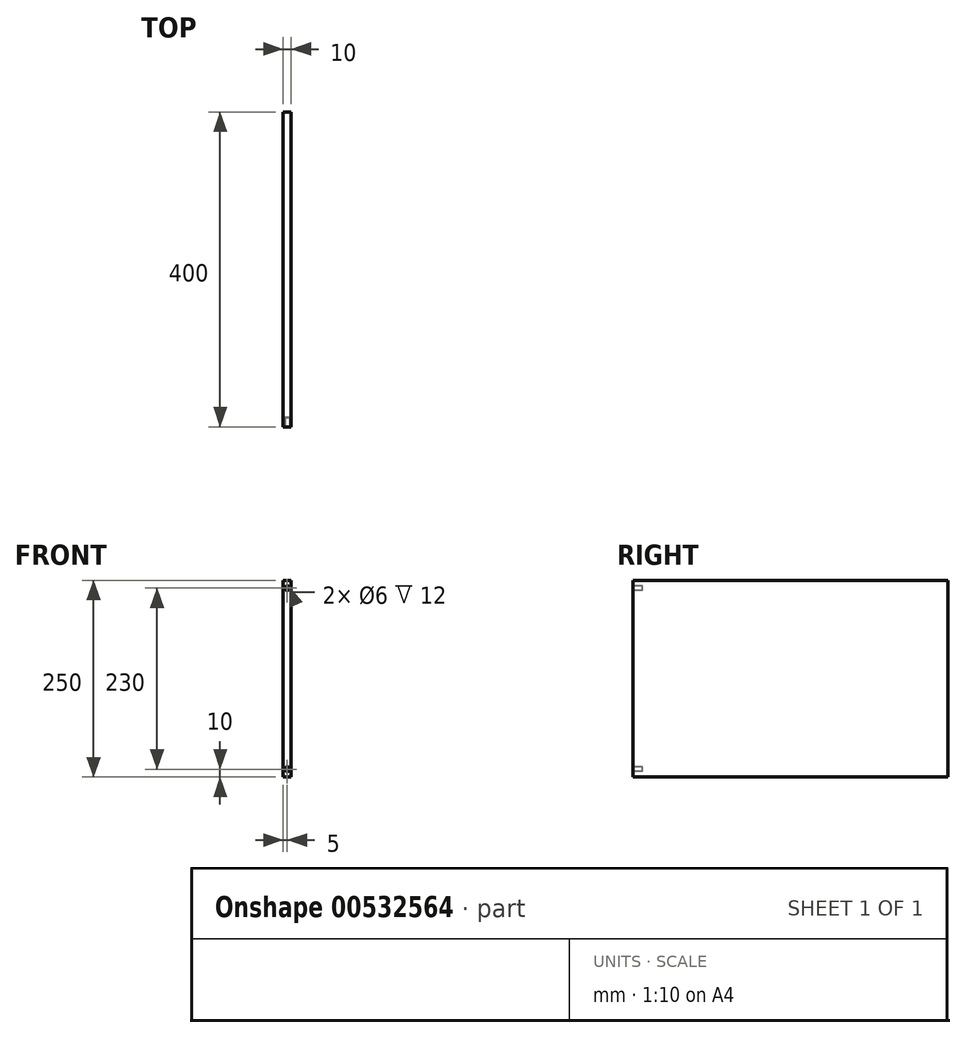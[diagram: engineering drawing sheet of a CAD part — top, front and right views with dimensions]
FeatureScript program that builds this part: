
annotation { "Feature Type Name" : "Feature", "Feature Type Description" : "" }
export const myFeature = defineFeature(function(context is Context, id is Id, definition is map)
    precondition{}
    {
        {
            var Q0;
            Q0=qCreatedBy(makeId("Right.planeOp"),FACE);
            var sketch = newSketch(context, id + "F0", { "sketchPlane" : qUnion([Q0])});
            skLineSegment(sketch, "E0.bottom", {"start": v(0, 0) * mm, "end": v(400, 0) * mm});
            skLineSegment(sketch, "E0.top", {"start": v(0, 250) * mm, "end": v(400, 250) * mm});
            skLineSegment(sketch, "E0.left", {"start": v(0, 0) * mm, "end": v(0, 250) * mm});
            skLineSegment(sketch, "E0.right", {"start": v(400, 0) * mm, "end": v(400, 250) * mm});
            skSolve(sketch);
        }
        {
            var Q0;
            Q0 = qSketchRegion(id + "F0", true);
            extrude(context, id + "F1", {"entities" : qUnion([Q0]), "depth" : 10 * mm, "offsetDistance" : 25 * mm});
        }
        {
            var Q0;
            Q0=makeQuery(id+"F1.opExtrude","SWEPT_FACE",FACE,{"disambiguationData":[OSD([sQuery(id+"F0.wireOp",EDGE,"E0.left")])]});
            var sketch = newSketch(context, id + "F2", { "sketchPlane" : qUnion([Q0])});
            skCircle(sketch, "E1", {"center": v(5, 240) * mm, "radius": 3 * mm});
            skCircle(sketch, "E2", {"center": v(5, 10) * mm, "radius": 3 * mm});
            skSolve(sketch);
        }
        {
            var Q0;
            Q0 = qSketchRegion(id + "F2", true);
            extrude(context, id + "F3", {"entities" : qUnion([Q0]), "operationType" : NewBodyOperationType.REMOVE, "oppositeDirection" : true, "depth" : 12 * mm, "offsetDistance" : 25 * mm});
        }
    });
